# Revit family: Accessory-Handshower_Holder-KOHLER-Loure-K-14789
name_source: partatom
category: Specialty Equipment
revit_build: Autodesk Revit 2015 (Build: 20140606_1530(x64)
units: mm (PartAtom-declared; Revit-internal decimal feet)

## types (5) — shared parameters
ADA Compliant = No
Assembly Code = C1030200
Date Modified = 02/27/2019
Default Elevation = 0"
Description = Deck-Mount Handshower Holder
Height = 1 13/16"
Length = 2 1/8"
Manufacturer = KOHLER Co.
MasterFormat 1995 = 15410
MasterFormat 2004 = 22.41.23
Material = Durable Metal Construction
Product Documentation Link = https://www.us.kohler.com
Product Name = Loure
Product Page URL = http://www.us.kohler.com
URL = https://www.us.kohler.com
WaterSense Certified = No
Width = 2 1/8"

## per-type parameters (varying)
| type | Finish | Model | Type |
| CP-Polished Chrome | Kohler-Metal-CP-Polished_Chrome | K-14789-CP | 1 |
| SN-Vibrant Polished Nickel | Kohler-Metal-SN-Vibrant_Polished_Nickel | K-14789-SN | 2 |
| BGD-Vibrant Moderne Brushed Gold | Kohler-Metal-BGD-Vibrant_Moderne_Brushed_Gold | K-14789-BGD | 4 |
| BN-Vibrant Brushed Nickel | Kohler-Metal-BN-Vibrant_Brushed_Nickel | K-14789-BN | 3 |
| TT-Titanium | Kohler-Metal-TT-Vibrant_Titanium | K-14789-TT | 5 |

## geometry (parser evidence)
native form markers: Sweep x7
no freeform markers — native parametric forms only
